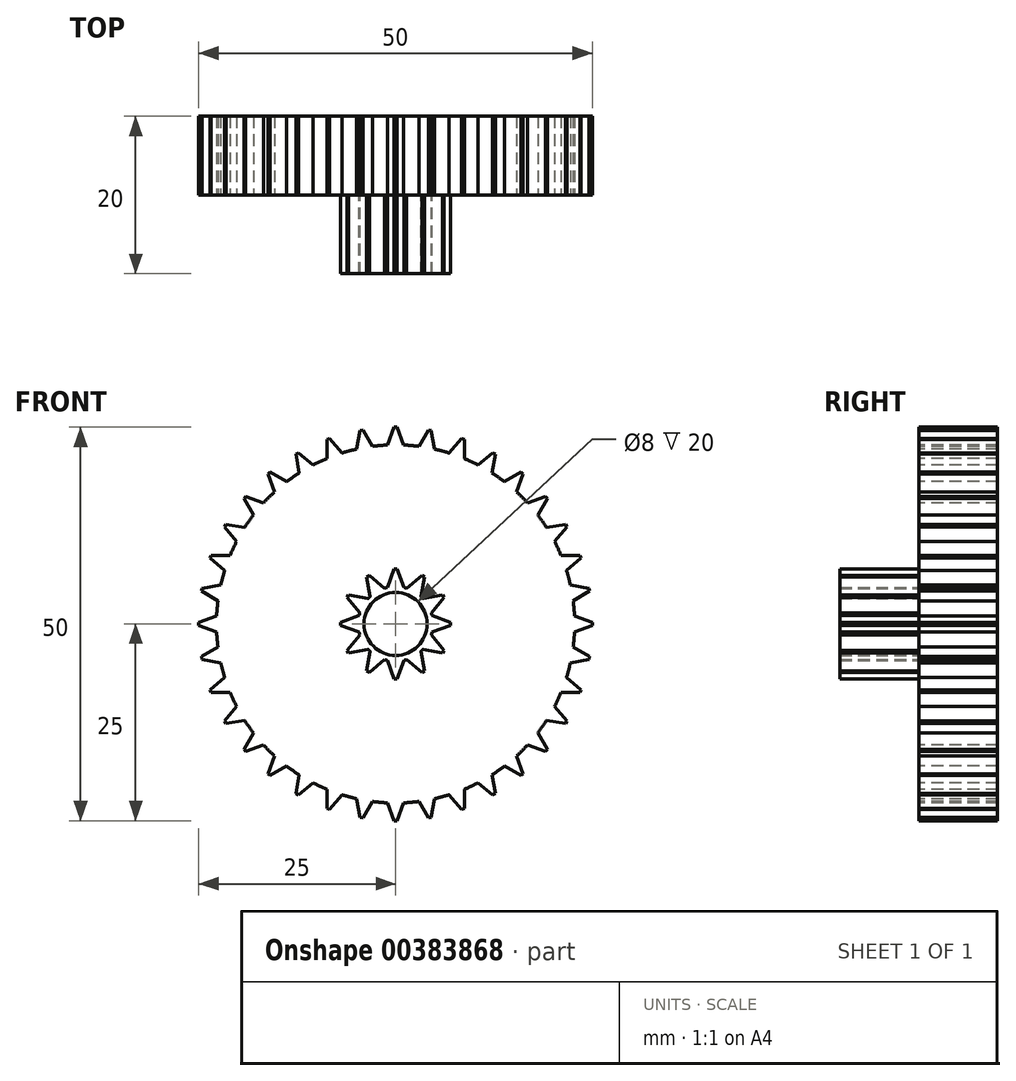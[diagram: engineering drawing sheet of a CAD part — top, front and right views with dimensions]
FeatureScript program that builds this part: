
annotation { "Feature Type Name" : "Feature", "Feature Type Description" : "" }
export const myFeature = defineFeature(function(context is Context, id is Id, definition is map)
    precondition{}
    {
        {
            var Q0;
            Q0=qCreatedBy(makeId("Front.planeOp"),FACE);
            var sketch = newSketch(context, id + "F0", { "sketchPlane" : qUnion([Q0])});
            skCircle(sketch, "E0", {"center": v(0, 0) * mm, "radius": 4 * mm});
            skCircle(sketch, "E1", {"center": v(0, 0) * mm, "radius": 4.75 * mm});
            skCircle(sketch, "E2", {"center": v(0, 0) * mm, "radius": 7 * mm, "construction": true});
            skLineSegment(sketch, "E3", {"start": v(-1.05, 4.63) * mm, "end": v(-0.19, 7) * mm});
            skLineSegment(sketch, "E4", {"start": v(-0.19, 7) * mm, "end": v(0, 7) * mm});
            skLineSegment(sketch, "E5", {"start": v(-1.05, 4.63) * mm, "end": v(-1.05, 7.84) * mm, "construction": true});
            skLineSegment(sketch, "E6.MirrorCS", {"start": v(0.19, 7) * mm, "end": v(0, 7) * mm});
            skLineSegment(sketch, "E7.MirrorCS", {"start": v(1.05, 4.63) * mm, "end": v(0.19, 7) * mm});
            skLineSegment(sketch, "E8.1.0", {"start": v(-3.22, 3.49) * mm, "end": v(-3.66, 5.97) * mm});
            skLineSegment(sketch, "E8.1.1", {"start": v(-3.66, 5.97) * mm, "end": v(-3.5, 6.06) * mm});
            skLineSegment(sketch, "E8.1.2", {"start": v(-3.34, 6.16) * mm, "end": v(-3.5, 6.06) * mm});
            skLineSegment(sketch, "E8.1.3", {"start": v(-1.4, 4.54) * mm, "end": v(-3.34, 6.16) * mm});
            skLineSegment(sketch, "E8.2.0", {"start": v(-4.54, 1.4) * mm, "end": v(-6.16, 3.34) * mm});
            skLineSegment(sketch, "E8.2.1", {"start": v(-6.16, 3.34) * mm, "end": v(-6.06, 3.5) * mm});
            skLineSegment(sketch, "E8.2.2", {"start": v(-5.97, 3.66) * mm, "end": v(-6.06, 3.5) * mm});
            skLineSegment(sketch, "E8.2.3", {"start": v(-3.49, 3.22) * mm, "end": v(-5.97, 3.66) * mm});
            skLineSegment(sketch, "E8.3.0", {"start": v(-4.63, -1.05) * mm, "end": v(-7, -0.19) * mm});
            skLineSegment(sketch, "E8.3.1", {"start": v(-7, -0.19) * mm, "end": v(-7, 0) * mm});
            skLineSegment(sketch, "E8.3.2", {"start": v(-7, 0.19) * mm, "end": v(-7, 0) * mm});
            skLineSegment(sketch, "E8.3.3", {"start": v(-4.63, 1.05) * mm, "end": v(-7, 0.19) * mm});
            skLineSegment(sketch, "E8.4.0", {"start": v(-3.49, -3.22) * mm, "end": v(-5.97, -3.66) * mm});
            skLineSegment(sketch, "E8.4.1", {"start": v(-5.97, -3.66) * mm, "end": v(-6.06, -3.5) * mm});
            skLineSegment(sketch, "E8.4.2", {"start": v(-6.16, -3.34) * mm, "end": v(-6.06, -3.5) * mm});
            skLineSegment(sketch, "E8.4.3", {"start": v(-4.54, -1.4) * mm, "end": v(-6.16, -3.34) * mm});
            skLineSegment(sketch, "E8.5.0", {"start": v(-1.4, -4.54) * mm, "end": v(-3.34, -6.16) * mm});
            skLineSegment(sketch, "E8.5.1", {"start": v(-3.34, -6.16) * mm, "end": v(-3.5, -6.06) * mm});
            skLineSegment(sketch, "E8.5.2", {"start": v(-3.66, -5.97) * mm, "end": v(-3.5, -6.06) * mm});
            skLineSegment(sketch, "E8.5.3", {"start": v(-3.22, -3.49) * mm, "end": v(-3.66, -5.97) * mm});
            skLineSegment(sketch, "E8.6.0", {"start": v(1.05, -4.63) * mm, "end": v(0.19, -7) * mm});
            skLineSegment(sketch, "E8.6.1", {"start": v(0.19, -7) * mm, "end": v(0, -7) * mm});
            skLineSegment(sketch, "E8.6.2", {"start": v(-0.19, -7) * mm, "end": v(0, -7) * mm});
            skLineSegment(sketch, "E8.6.3", {"start": v(-1.05, -4.63) * mm, "end": v(-0.19, -7) * mm});
            skLineSegment(sketch, "E8.7.0", {"start": v(3.22, -3.49) * mm, "end": v(3.66, -5.97) * mm});
            skLineSegment(sketch, "E8.7.1", {"start": v(3.66, -5.97) * mm, "end": v(3.5, -6.06) * mm});
            skLineSegment(sketch, "E8.7.2", {"start": v(3.34, -6.16) * mm, "end": v(3.5, -6.06) * mm});
            skLineSegment(sketch, "E8.7.3", {"start": v(1.4, -4.54) * mm, "end": v(3.34, -6.16) * mm});
            skLineSegment(sketch, "E8.8.0", {"start": v(4.54, -1.4) * mm, "end": v(6.16, -3.34) * mm});
            skLineSegment(sketch, "E8.8.1", {"start": v(6.16, -3.34) * mm, "end": v(6.06, -3.5) * mm});
            skLineSegment(sketch, "E8.8.2", {"start": v(5.97, -3.66) * mm, "end": v(6.06, -3.5) * mm});
            skLineSegment(sketch, "E8.8.3", {"start": v(3.49, -3.22) * mm, "end": v(5.97, -3.66) * mm});
            skLineSegment(sketch, "E8.9.0", {"start": v(4.63, 1.05) * mm, "end": v(7, 0.19) * mm});
            skLineSegment(sketch, "E8.9.1", {"start": v(7, 0.19) * mm, "end": v(7, 0) * mm});
            skLineSegment(sketch, "E8.9.2", {"start": v(7, -0.19) * mm, "end": v(7, 0) * mm});
            skLineSegment(sketch, "E8.9.3", {"start": v(4.63, -1.05) * mm, "end": v(7, -0.19) * mm});
            skLineSegment(sketch, "E8.10.0", {"start": v(3.49, 3.22) * mm, "end": v(5.97, 3.66) * mm});
            skLineSegment(sketch, "E8.10.1", {"start": v(5.97, 3.66) * mm, "end": v(6.06, 3.5) * mm});
            skLineSegment(sketch, "E8.10.2", {"start": v(6.16, 3.34) * mm, "end": v(6.06, 3.5) * mm});
            skLineSegment(sketch, "E8.10.3", {"start": v(4.54, 1.4) * mm, "end": v(6.16, 3.34) * mm});
            skLineSegment(sketch, "E8.11.0", {"start": v(1.4, 4.54) * mm, "end": v(3.34, 6.16) * mm});
            skLineSegment(sketch, "E8.11.1", {"start": v(3.34, 6.16) * mm, "end": v(3.5, 6.06) * mm});
            skLineSegment(sketch, "E8.11.2", {"start": v(3.66, 5.97) * mm, "end": v(3.5, 6.06) * mm});
            skLineSegment(sketch, "E8.11.3", {"start": v(3.22, 3.49) * mm, "end": v(3.66, 5.97) * mm});
            skSolve(sketch);
        }
        {
            var Q0;
            Q0=qSketchRegion(id+"F0",true);
            extrude(context, id + "F1", {"entities" : qUnion([Q0]), "depth" : 10 * mm});
        }
        {
            var Q0;
            Q0=qCreatedBy(makeId("Front.planeOp"),FACE);
            var sketch = newSketch(context, id + "F2", { "sketchPlane" : qUnion([Q0])});
            skCircle(sketch, "E9", {"center": v(0, 0) * mm, "radius": 4 * mm});
            skCircle(sketch, "E10", {"center": v(0, 0) * mm, "radius": 22.75 * mm});
            skCircle(sketch, "E11", {"center": v(0, 0) * mm, "radius": 25 * mm, "construction": true});
            skLineSegment(sketch, "E12", {"start": v(-1.01, 22.73) * mm, "end": v(-0.19, 25) * mm});
            skLineSegment(sketch, "E13", {"start": v(-0.19, 25) * mm, "end": v(0, 25) * mm});
            skLineSegment(sketch, "E14", {"start": v(-1.01, 22.73) * mm, "end": v(-1.01, 31.54) * mm, "construction": true});
            skLineSegment(sketch, "E15.MirrorCS", {"start": v(0.19, 25) * mm, "end": v(0, 25) * mm});
            skLineSegment(sketch, "E16.MirrorCS", {"start": v(1.01, 22.73) * mm, "end": v(0.19, 25) * mm});
            skLineSegment(sketch, "E17.1.0", {"start": v(-4.95, 22.2) * mm, "end": v(-4.53, 24.59) * mm});
            skLineSegment(sketch, "E17.1.1", {"start": v(-4.16, 24.65) * mm, "end": v(-4.34, 24.62) * mm});
            skLineSegment(sketch, "E17.1.2", {"start": v(-4.53, 24.59) * mm, "end": v(-4.34, 24.62) * mm});
            skLineSegment(sketch, "E17.1.3", {"start": v(-2.95, 22.56) * mm, "end": v(-4.16, 24.65) * mm});
            skLineSegment(sketch, "E17.2.0", {"start": v(-8.73, 21) * mm, "end": v(-8.73, 23.43) * mm});
            skLineSegment(sketch, "E17.2.1", {"start": v(-8.37, 23.56) * mm, "end": v(-8.55, 23.5) * mm});
            skLineSegment(sketch, "E17.2.2", {"start": v(-8.73, 23.43) * mm, "end": v(-8.55, 23.5) * mm});
            skLineSegment(sketch, "E17.2.3", {"start": v(-6.82, 21.7) * mm, "end": v(-8.37, 23.56) * mm});
            skLineSegment(sketch, "E17.3.0", {"start": v(-12.24, 19.18) * mm, "end": v(-12.66, 21.56) * mm});
            skLineSegment(sketch, "E17.3.1", {"start": v(-12.34, 21.74) * mm, "end": v(-12.5, 21.65) * mm});
            skLineSegment(sketch, "E17.3.2", {"start": v(-12.66, 21.56) * mm, "end": v(-12.5, 21.65) * mm});
            skLineSegment(sketch, "E17.3.3", {"start": v(-10.48, 20.19) * mm, "end": v(-12.34, 21.74) * mm});
            skLineSegment(sketch, "E17.4.0", {"start": v(-15.39, 16.76) * mm, "end": v(-16.21, 19.03) * mm});
            skLineSegment(sketch, "E17.4.1", {"start": v(-15.93, 19.27) * mm, "end": v(-16.07, 19.15) * mm});
            skLineSegment(sketch, "E17.4.2", {"start": v(-16.21, 19.03) * mm, "end": v(-16.07, 19.15) * mm});
            skLineSegment(sketch, "E17.4.3", {"start": v(-13.83, 18.06) * mm, "end": v(-15.93, 19.27) * mm});
            skLineSegment(sketch, "E17.5.0", {"start": v(-18.06, 13.83) * mm, "end": v(-19.27, 15.93) * mm});
            skLineSegment(sketch, "E17.5.1", {"start": v(-19.03, 16.21) * mm, "end": v(-19.15, 16.07) * mm});
            skLineSegment(sketch, "E17.5.2", {"start": v(-19.27, 15.93) * mm, "end": v(-19.15, 16.07) * mm});
            skLineSegment(sketch, "E17.5.3", {"start": v(-16.76, 15.39) * mm, "end": v(-19.03, 16.21) * mm});
            skLineSegment(sketch, "E17.6.0", {"start": v(-20.19, 10.48) * mm, "end": v(-21.74, 12.34) * mm});
            skLineSegment(sketch, "E17.6.1", {"start": v(-21.56, 12.66) * mm, "end": v(-21.65, 12.5) * mm});
            skLineSegment(sketch, "E17.6.2", {"start": v(-21.74, 12.34) * mm, "end": v(-21.65, 12.5) * mm});
            skLineSegment(sketch, "E17.6.3", {"start": v(-19.18, 12.24) * mm, "end": v(-21.56, 12.66) * mm});
            skLineSegment(sketch, "E17.7.0", {"start": v(-21.7, 6.82) * mm, "end": v(-23.56, 8.37) * mm});
            skLineSegment(sketch, "E17.7.1", {"start": v(-23.43, 8.73) * mm, "end": v(-23.5, 8.55) * mm});
            skLineSegment(sketch, "E17.7.2", {"start": v(-23.56, 8.37) * mm, "end": v(-23.5, 8.55) * mm});
            skLineSegment(sketch, "E17.7.3", {"start": v(-21, 8.73) * mm, "end": v(-23.43, 8.73) * mm});
            skLineSegment(sketch, "E17.8.0", {"start": v(-22.56, 2.95) * mm, "end": v(-24.65, 4.16) * mm});
            skLineSegment(sketch, "E17.8.1", {"start": v(-24.59, 4.53) * mm, "end": v(-24.62, 4.34) * mm});
            skLineSegment(sketch, "E17.8.2", {"start": v(-24.65, 4.16) * mm, "end": v(-24.62, 4.34) * mm});
            skLineSegment(sketch, "E17.8.3", {"start": v(-22.2, 4.95) * mm, "end": v(-24.59, 4.53) * mm});
            skLineSegment(sketch, "E17.9.0", {"start": v(-22.73, -1.01) * mm, "end": v(-25, -0.19) * mm});
            skLineSegment(sketch, "E17.9.1", {"start": v(-25, 0.19) * mm, "end": v(-25, 0) * mm});
            skLineSegment(sketch, "E17.9.2", {"start": v(-25, -0.19) * mm, "end": v(-25, 0) * mm});
            skLineSegment(sketch, "E17.9.3", {"start": v(-22.73, 1.01) * mm, "end": v(-25, 0.19) * mm});
            skLineSegment(sketch, "E17.10.0", {"start": v(-22.2, -4.95) * mm, "end": v(-24.59, -4.53) * mm});
            skLineSegment(sketch, "E17.10.1", {"start": v(-24.65, -4.16) * mm, "end": v(-24.62, -4.34) * mm});
            skLineSegment(sketch, "E17.10.2", {"start": v(-24.59, -4.53) * mm, "end": v(-24.62, -4.34) * mm});
            skLineSegment(sketch, "E17.10.3", {"start": v(-22.56, -2.95) * mm, "end": v(-24.65, -4.16) * mm});
            skLineSegment(sketch, "E17.11.0", {"start": v(-21, -8.73) * mm, "end": v(-23.43, -8.73) * mm});
            skLineSegment(sketch, "E17.11.1", {"start": v(-23.56, -8.37) * mm, "end": v(-23.5, -8.55) * mm});
            skLineSegment(sketch, "E17.11.2", {"start": v(-23.43, -8.73) * mm, "end": v(-23.5, -8.55) * mm});
            skLineSegment(sketch, "E17.11.3", {"start": v(-21.7, -6.82) * mm, "end": v(-23.56, -8.37) * mm});
            skLineSegment(sketch, "E17.12.0", {"start": v(-19.18, -12.24) * mm, "end": v(-21.56, -12.66) * mm});
            skLineSegment(sketch, "E17.12.1", {"start": v(-21.74, -12.34) * mm, "end": v(-21.65, -12.5) * mm});
            skLineSegment(sketch, "E17.12.2", {"start": v(-21.56, -12.66) * mm, "end": v(-21.65, -12.5) * mm});
            skLineSegment(sketch, "E17.12.3", {"start": v(-20.19, -10.48) * mm, "end": v(-21.74, -12.34) * mm});
            skLineSegment(sketch, "E17.13.0", {"start": v(-16.76, -15.39) * mm, "end": v(-19.03, -16.21) * mm});
            skLineSegment(sketch, "E17.13.1", {"start": v(-19.27, -15.93) * mm, "end": v(-19.15, -16.07) * mm});
            skLineSegment(sketch, "E17.13.2", {"start": v(-19.03, -16.21) * mm, "end": v(-19.15, -16.07) * mm});
            skLineSegment(sketch, "E17.13.3", {"start": v(-18.06, -13.83) * mm, "end": v(-19.27, -15.93) * mm});
            skLineSegment(sketch, "E17.14.0", {"start": v(-13.83, -18.06) * mm, "end": v(-15.93, -19.27) * mm});
            skLineSegment(sketch, "E17.14.1", {"start": v(-16.21, -19.03) * mm, "end": v(-16.07, -19.15) * mm});
            skLineSegment(sketch, "E17.14.2", {"start": v(-15.93, -19.27) * mm, "end": v(-16.07, -19.15) * mm});
            skLineSegment(sketch, "E17.14.3", {"start": v(-15.39, -16.76) * mm, "end": v(-16.21, -19.03) * mm});
            skLineSegment(sketch, "E17.15.0", {"start": v(-10.48, -20.19) * mm, "end": v(-12.34, -21.74) * mm});
            skLineSegment(sketch, "E17.15.1", {"start": v(-12.66, -21.56) * mm, "end": v(-12.5, -21.65) * mm});
            skLineSegment(sketch, "E17.15.2", {"start": v(-12.34, -21.74) * mm, "end": v(-12.5, -21.65) * mm});
            skLineSegment(sketch, "E17.15.3", {"start": v(-12.24, -19.18) * mm, "end": v(-12.66, -21.56) * mm});
            skLineSegment(sketch, "E17.16.0", {"start": v(-6.82, -21.7) * mm, "end": v(-8.37, -23.56) * mm});
            skLineSegment(sketch, "E17.16.1", {"start": v(-8.73, -23.43) * mm, "end": v(-8.55, -23.5) * mm});
            skLineSegment(sketch, "E17.16.2", {"start": v(-8.37, -23.56) * mm, "end": v(-8.55, -23.5) * mm});
            skLineSegment(sketch, "E17.16.3", {"start": v(-8.73, -21) * mm, "end": v(-8.73, -23.43) * mm});
            skLineSegment(sketch, "E17.17.0", {"start": v(-2.95, -22.56) * mm, "end": v(-4.16, -24.65) * mm});
            skLineSegment(sketch, "E17.17.1", {"start": v(-4.53, -24.59) * mm, "end": v(-4.34, -24.62) * mm});
            skLineSegment(sketch, "E17.17.2", {"start": v(-4.16, -24.65) * mm, "end": v(-4.34, -24.62) * mm});
            skLineSegment(sketch, "E17.17.3", {"start": v(-4.95, -22.2) * mm, "end": v(-4.53, -24.59) * mm});
            skLineSegment(sketch, "E17.18.0", {"start": v(1.01, -22.73) * mm, "end": v(0.19, -25) * mm});
            skLineSegment(sketch, "E17.18.1", {"start": v(-0.19, -25) * mm, "end": v(0, -25) * mm});
            skLineSegment(sketch, "E17.18.2", {"start": v(0.19, -25) * mm, "end": v(0, -25) * mm});
            skLineSegment(sketch, "E17.18.3", {"start": v(-1.01, -22.73) * mm, "end": v(-0.19, -25) * mm});
            skLineSegment(sketch, "E17.19.0", {"start": v(4.95, -22.2) * mm, "end": v(4.53, -24.59) * mm});
            skLineSegment(sketch, "E17.19.1", {"start": v(4.16, -24.65) * mm, "end": v(4.34, -24.62) * mm});
            skLineSegment(sketch, "E17.19.2", {"start": v(4.53, -24.59) * mm, "end": v(4.34, -24.62) * mm});
            skLineSegment(sketch, "E17.19.3", {"start": v(2.95, -22.56) * mm, "end": v(4.16, -24.65) * mm});
            skLineSegment(sketch, "E17.20.0", {"start": v(8.73, -21) * mm, "end": v(8.73, -23.43) * mm});
            skLineSegment(sketch, "E17.20.1", {"start": v(8.37, -23.56) * mm, "end": v(8.55, -23.5) * mm});
            skLineSegment(sketch, "E17.20.2", {"start": v(8.73, -23.43) * mm, "end": v(8.55, -23.5) * mm});
            skLineSegment(sketch, "E17.20.3", {"start": v(6.82, -21.7) * mm, "end": v(8.37, -23.56) * mm});
            skLineSegment(sketch, "E17.21.0", {"start": v(12.24, -19.18) * mm, "end": v(12.66, -21.56) * mm});
            skLineSegment(sketch, "E17.21.1", {"start": v(12.34, -21.74) * mm, "end": v(12.5, -21.65) * mm});
            skLineSegment(sketch, "E17.21.2", {"start": v(12.66, -21.56) * mm, "end": v(12.5, -21.65) * mm});
            skLineSegment(sketch, "E17.21.3", {"start": v(10.48, -20.19) * mm, "end": v(12.34, -21.74) * mm});
            skLineSegment(sketch, "E17.22.0", {"start": v(15.39, -16.76) * mm, "end": v(16.21, -19.03) * mm});
            skLineSegment(sketch, "E17.22.1", {"start": v(15.93, -19.27) * mm, "end": v(16.07, -19.15) * mm});
            skLineSegment(sketch, "E17.22.2", {"start": v(16.21, -19.03) * mm, "end": v(16.07, -19.15) * mm});
            skLineSegment(sketch, "E17.22.3", {"start": v(13.83, -18.06) * mm, "end": v(15.93, -19.27) * mm});
            skLineSegment(sketch, "E17.23.0", {"start": v(18.06, -13.83) * mm, "end": v(19.27, -15.93) * mm});
            skLineSegment(sketch, "E17.23.1", {"start": v(19.03, -16.21) * mm, "end": v(19.15, -16.07) * mm});
            skLineSegment(sketch, "E17.23.2", {"start": v(19.27, -15.93) * mm, "end": v(19.15, -16.07) * mm});
            skLineSegment(sketch, "E17.23.3", {"start": v(16.76, -15.39) * mm, "end": v(19.03, -16.21) * mm});
            skLineSegment(sketch, "E17.24.0", {"start": v(20.19, -10.48) * mm, "end": v(21.74, -12.34) * mm});
            skLineSegment(sketch, "E17.24.1", {"start": v(21.56, -12.66) * mm, "end": v(21.65, -12.5) * mm});
            skLineSegment(sketch, "E17.24.2", {"start": v(21.74, -12.34) * mm, "end": v(21.65, -12.5) * mm});
            skLineSegment(sketch, "E17.24.3", {"start": v(19.18, -12.24) * mm, "end": v(21.56, -12.66) * mm});
            skLineSegment(sketch, "E17.25.0", {"start": v(21.7, -6.82) * mm, "end": v(23.56, -8.37) * mm});
            skLineSegment(sketch, "E17.25.1", {"start": v(23.43, -8.73) * mm, "end": v(23.5, -8.55) * mm});
            skLineSegment(sketch, "E17.25.2", {"start": v(23.56, -8.37) * mm, "end": v(23.5, -8.55) * mm});
            skLineSegment(sketch, "E17.25.3", {"start": v(21, -8.73) * mm, "end": v(23.43, -8.73) * mm});
            skLineSegment(sketch, "E17.26.0", {"start": v(22.56, -2.95) * mm, "end": v(24.65, -4.16) * mm});
            skLineSegment(sketch, "E17.26.1", {"start": v(24.59, -4.53) * mm, "end": v(24.62, -4.34) * mm});
            skLineSegment(sketch, "E17.26.2", {"start": v(24.65, -4.16) * mm, "end": v(24.62, -4.34) * mm});
            skLineSegment(sketch, "E17.26.3", {"start": v(22.2, -4.95) * mm, "end": v(24.59, -4.53) * mm});
            skLineSegment(sketch, "E17.27.0", {"start": v(22.73, 1.01) * mm, "end": v(25, 0.19) * mm});
            skLineSegment(sketch, "E17.27.1", {"start": v(25, -0.19) * mm, "end": v(25, 0) * mm});
            skLineSegment(sketch, "E17.27.2", {"start": v(25, 0.19) * mm, "end": v(25, 0) * mm});
            skLineSegment(sketch, "E17.27.3", {"start": v(22.73, -1.01) * mm, "end": v(25, -0.19) * mm});
            skLineSegment(sketch, "E17.28.0", {"start": v(22.2, 4.95) * mm, "end": v(24.59, 4.53) * mm});
            skLineSegment(sketch, "E17.28.1", {"start": v(24.65, 4.16) * mm, "end": v(24.62, 4.34) * mm});
            skLineSegment(sketch, "E17.28.2", {"start": v(24.59, 4.53) * mm, "end": v(24.62, 4.34) * mm});
            skLineSegment(sketch, "E17.28.3", {"start": v(22.56, 2.95) * mm, "end": v(24.65, 4.16) * mm});
            skLineSegment(sketch, "E17.29.0", {"start": v(21, 8.73) * mm, "end": v(23.43, 8.73) * mm});
            skLineSegment(sketch, "E17.29.1", {"start": v(23.56, 8.37) * mm, "end": v(23.5, 8.55) * mm});
            skLineSegment(sketch, "E17.29.2", {"start": v(23.43, 8.73) * mm, "end": v(23.5, 8.55) * mm});
            skLineSegment(sketch, "E17.29.3", {"start": v(21.7, 6.82) * mm, "end": v(23.56, 8.37) * mm});
            skLineSegment(sketch, "E17.30.0", {"start": v(19.18, 12.24) * mm, "end": v(21.56, 12.66) * mm});
            skLineSegment(sketch, "E17.30.1", {"start": v(21.74, 12.34) * mm, "end": v(21.65, 12.5) * mm});
            skLineSegment(sketch, "E17.30.2", {"start": v(21.56, 12.66) * mm, "end": v(21.65, 12.5) * mm});
            skLineSegment(sketch, "E17.30.3", {"start": v(20.19, 10.48) * mm, "end": v(21.74, 12.34) * mm});
            skLineSegment(sketch, "E17.31.0", {"start": v(16.76, 15.39) * mm, "end": v(19.03, 16.21) * mm});
            skLineSegment(sketch, "E17.31.1", {"start": v(19.27, 15.93) * mm, "end": v(19.15, 16.07) * mm});
            skLineSegment(sketch, "E17.31.2", {"start": v(19.03, 16.21) * mm, "end": v(19.15, 16.07) * mm});
            skLineSegment(sketch, "E17.31.3", {"start": v(18.06, 13.83) * mm, "end": v(19.27, 15.93) * mm});
            skLineSegment(sketch, "E17.32.0", {"start": v(13.83, 18.06) * mm, "end": v(15.93, 19.27) * mm});
            skLineSegment(sketch, "E17.32.1", {"start": v(16.21, 19.03) * mm, "end": v(16.07, 19.15) * mm});
            skLineSegment(sketch, "E17.32.2", {"start": v(15.93, 19.27) * mm, "end": v(16.07, 19.15) * mm});
            skLineSegment(sketch, "E17.32.3", {"start": v(15.39, 16.76) * mm, "end": v(16.21, 19.03) * mm});
            skLineSegment(sketch, "E17.33.0", {"start": v(10.48, 20.19) * mm, "end": v(12.34, 21.74) * mm});
            skLineSegment(sketch, "E17.33.1", {"start": v(12.66, 21.56) * mm, "end": v(12.5, 21.65) * mm});
            skLineSegment(sketch, "E17.33.2", {"start": v(12.34, 21.74) * mm, "end": v(12.5, 21.65) * mm});
            skLineSegment(sketch, "E17.33.3", {"start": v(12.24, 19.18) * mm, "end": v(12.66, 21.56) * mm});
            skLineSegment(sketch, "E17.34.0", {"start": v(6.82, 21.7) * mm, "end": v(8.37, 23.56) * mm});
            skLineSegment(sketch, "E17.34.1", {"start": v(8.73, 23.43) * mm, "end": v(8.55, 23.5) * mm});
            skLineSegment(sketch, "E17.34.2", {"start": v(8.37, 23.56) * mm, "end": v(8.55, 23.5) * mm});
            skLineSegment(sketch, "E17.34.3", {"start": v(8.73, 21) * mm, "end": v(8.73, 23.43) * mm});
            skLineSegment(sketch, "E17.35.0", {"start": v(2.95, 22.56) * mm, "end": v(4.16, 24.65) * mm});
            skLineSegment(sketch, "E17.35.1", {"start": v(4.53, 24.59) * mm, "end": v(4.34, 24.62) * mm});
            skLineSegment(sketch, "E17.35.2", {"start": v(4.16, 24.65) * mm, "end": v(4.34, 24.62) * mm});
            skLineSegment(sketch, "E17.35.3", {"start": v(4.95, 22.2) * mm, "end": v(4.53, 24.59) * mm});
            skSolve(sketch);
        }
        {
            var Q0;
            Q0=qSketchRegion(id+"F2",true);
            extrude(context, id + "F3", {"entities" : qUnion([Q0]), "operationType" : NewBodyOperationType.ADD, "depth" : -10 * mm});
        }
    });
